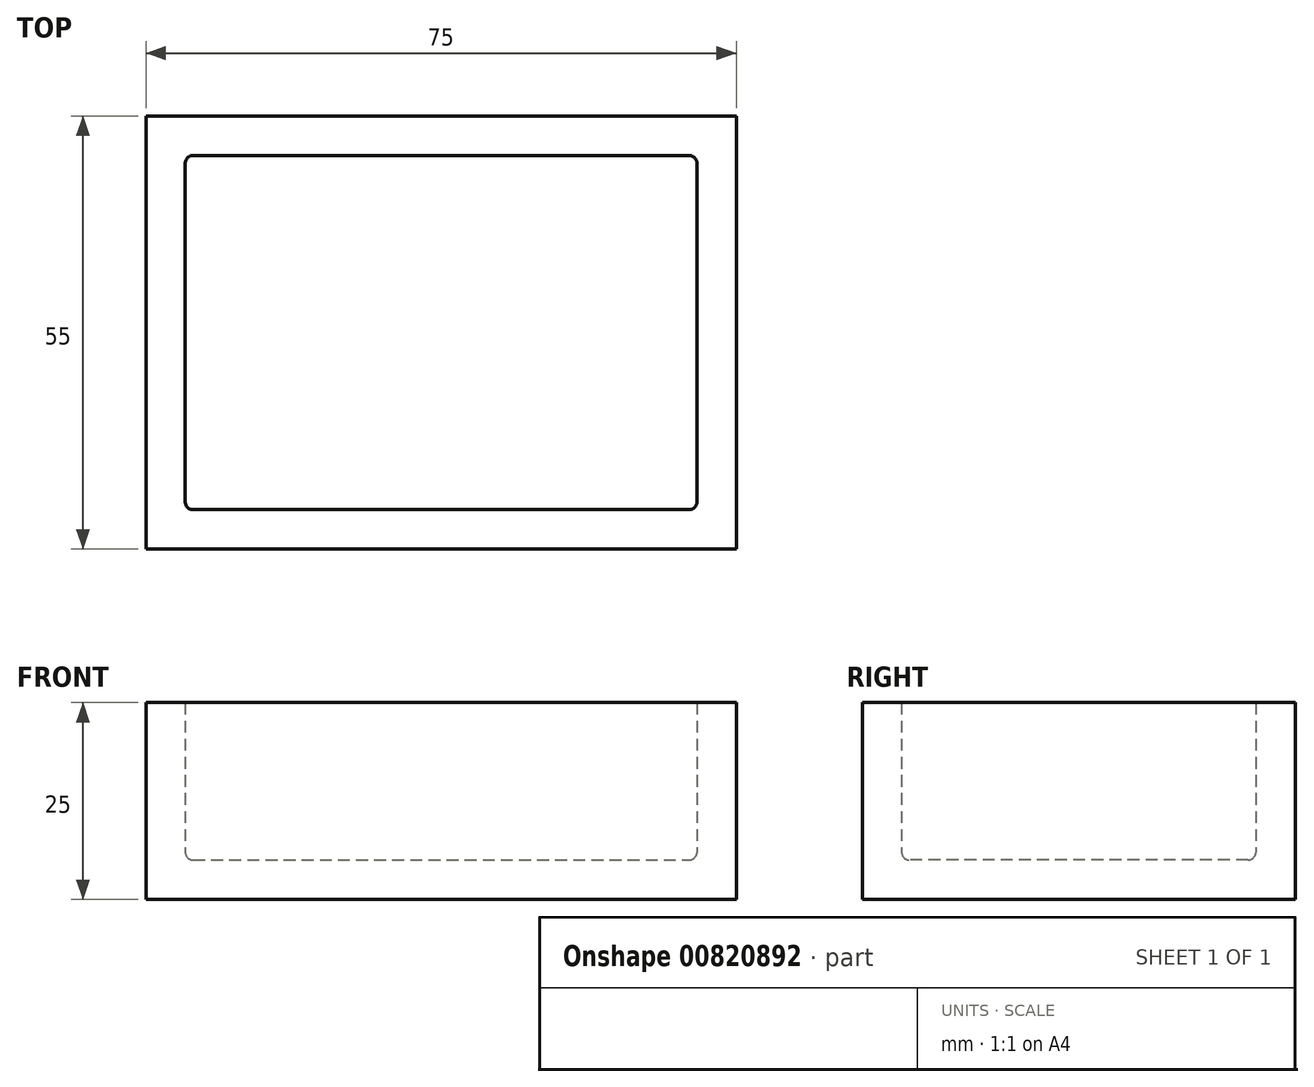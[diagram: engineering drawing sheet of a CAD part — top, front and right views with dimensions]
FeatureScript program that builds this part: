
annotation { "Feature Type Name" : "Feature", "Feature Type Description" : "" }
export const myFeature = defineFeature(function(context is Context, id is Id, definition is map)
    precondition{}
    {
        {
            var Q0;
            Q0=qCreatedBy(makeId("Top.planeOp"),FACE);
            var sketch = newSketch(context, id + "F0", { "sketchPlane" : qUnion([Q0])});
            skLineSegment(sketch, "E0.bottom", {"start": v(-32.5, 22.5) * mm, "end": v(32.5, 22.5) * mm});
            skLineSegment(sketch, "E0.top", {"start": v(-32.5, -22.5) * mm, "end": v(32.5, -22.5) * mm});
            skLineSegment(sketch, "E0.left", {"start": v(-32.5, 22.5) * mm, "end": v(-32.5, -22.5) * mm});
            skLineSegment(sketch, "E0.right", {"start": v(32.5, 22.5) * mm, "end": v(32.5, -22.5) * mm});
            skPoint(sketch, "E0.middle", {"position": v(0, 0) * mm});
            skSolve(sketch);
        }
        {
            var Q0;
            Q0=makeQuery(id+"F0.imprint","IMPRINT",FACE,{"disambiguationData":[TD([[makeQuery(id+"F0.imprint","IMPRINT",EDGE,{"derivedFrom":sQuery(id+"F0.wireOp",EDGE,"E0.bottom")}),-1.0]])]});
            extrude(context, id + "F1", {"entities" : qUnion([Q0]), "depth" : 20 * mm, "offsetDistance" : 25 * mm});
        }
        {
            var Q0;
            Q0=makeQuery(id+"F1.opExtrude","CAP_FACE",FACE,{"disambiguationData":[OSD([sQuery(id+"F0.wireOp",EDGE,"E0.bottom"),sQuery(id+"F0.wireOp",EDGE,"E0.top"),sQuery(id+"F0.wireOp",EDGE,"E0.left"),sQuery(id+"F0.wireOp",EDGE,"E0.right")])],"isStart":false});
            shell(context, id + "F2", {"entities" : qUnion([Q0]), "thickness" : 5 * mm, "oppositeDirection" : true});
        }
        {
            var Q0;
            {var subQ0=sQuery(id+"F0.wireOp",EDGE,"E0.left");Q0=makeQuery(id+"F2.opShell","OFFSET_EDGE",EDGE,{"disambiguationData":[OSD([subQ0]),TDD([makeQuery(id+"F1.opExtrude","CAP_EDGE",EDGE,{"disambiguationData":[OSD([subQ0])],"isStart":true})])]});}
            var Q1;
            Q1=makeQuery(id+"F2.opShell","OFFSET_EDGE",EDGE,{"disambiguationData":[OSD([sQuery(id+"F0.wireOp",EDGE,"E0.bottom"),sQuery(id+"F0.wireOp",EDGE,"E0.left")])]});
            var Q2;
            {var subQ0=sQuery(id+"F0.wireOp",EDGE,"E0.bottom");Q2=makeQuery(id+"F2.opShell","OFFSET_EDGE",EDGE,{"disambiguationData":[OSD([subQ0]),TDD([makeQuery(id+"F1.opExtrude","CAP_EDGE",EDGE,{"disambiguationData":[OSD([subQ0])],"isStart":true})])]});}
            var Q3;
            Q3=makeQuery(id+"F2.opShell","OFFSET_EDGE",EDGE,{"disambiguationData":[OSD([sQuery(id+"F0.wireOp",EDGE,"E0.top"),sQuery(id+"F0.wireOp",EDGE,"E0.left")])]});
            var Q4;
            {var subQ0=sQuery(id+"F0.wireOp",EDGE,"E0.top");Q4=makeQuery(id+"F2.opShell","OFFSET_EDGE",EDGE,{"disambiguationData":[OSD([subQ0]),TDD([makeQuery(id+"F1.opExtrude","CAP_EDGE",EDGE,{"disambiguationData":[OSD([subQ0])],"isStart":true})])]});}
            var Q5;
            Q5=makeQuery(id+"F2.opShell","OFFSET_EDGE",EDGE,{"disambiguationData":[OSD([sQuery(id+"F0.wireOp",EDGE,"E0.top"),sQuery(id+"F0.wireOp",EDGE,"E0.right")])]});
            var Q6;
            {var subQ0=sQuery(id+"F0.wireOp",EDGE,"E0.right");Q6=makeQuery(id+"F2.opShell","OFFSET_EDGE",EDGE,{"disambiguationData":[OSD([subQ0]),TDD([makeQuery(id+"F1.opExtrude","CAP_EDGE",EDGE,{"disambiguationData":[OSD([subQ0])],"isStart":true})])]});}
            var Q7;
            Q7=makeQuery(id+"F2.opShell","OFFSET_EDGE",EDGE,{"disambiguationData":[OSD([sQuery(id+"F0.wireOp",EDGE,"E0.bottom"),sQuery(id+"F0.wireOp",EDGE,"E0.right")])]});
            fillet(context, id + "F3", {"entities" : qUnion([Q0, Q1, Q2, Q3, Q4, Q5, Q6, Q7]), "radius" : 1 * mm, "allowEdgeOverflow" : false});
        }
    });
